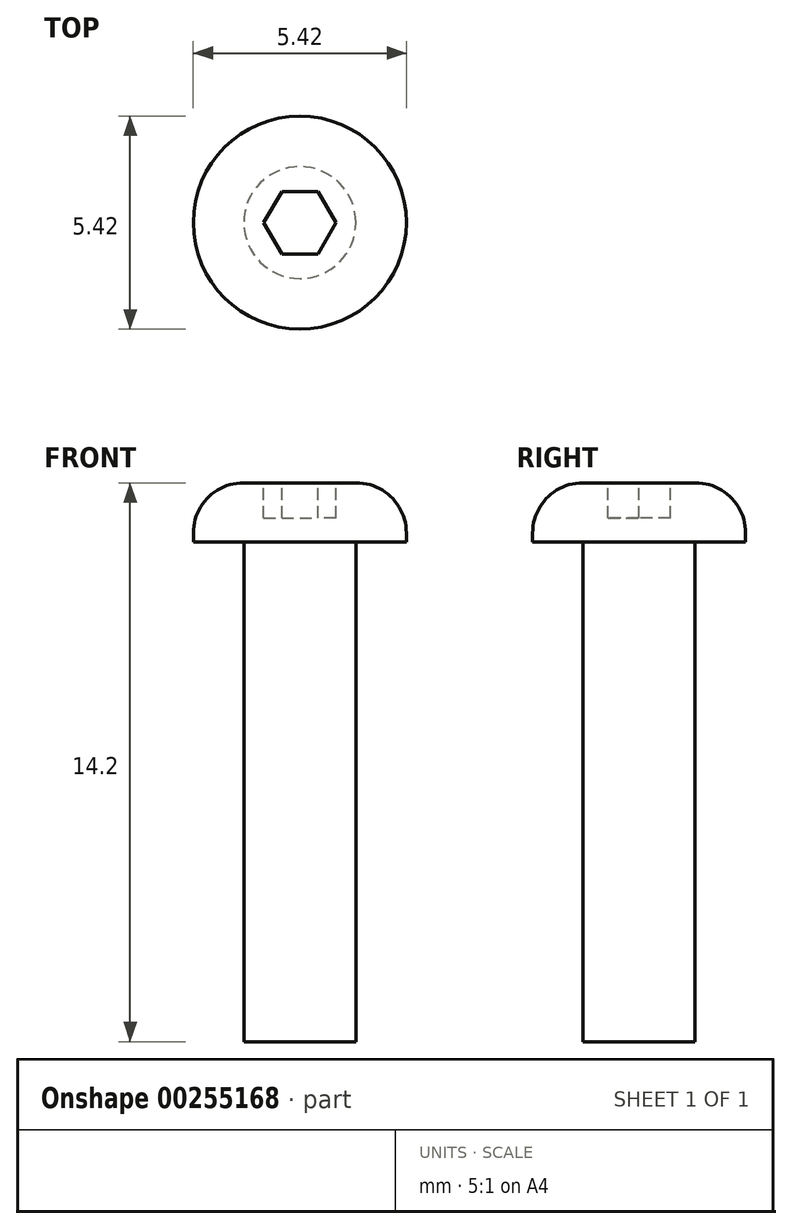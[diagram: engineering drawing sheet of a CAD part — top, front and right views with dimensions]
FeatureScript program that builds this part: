
annotation { "Feature Type Name" : "Feature", "Feature Type Description" : "" }
export const myFeature = defineFeature(function(context is Context, id is Id, definition is map)
    precondition{}
    {
        {
            var Q0;
            Q0=qCreatedBy(makeId("Top.planeOp"),FACE);
            var sketch = newSketch(context, id + "F0", { "sketchPlane" : qUnion([Q0])});
            skCircle(sketch, "E0", {"center": v(0, 0) * mm, "radius": 1.42 * mm});
            skSolve(sketch);
        }
        {
            var Q0;
            Q0 = qSketchRegion(id + "F0", true);
            extrude(context, id + "F1", {"entities" : qUnion([Q0]), "depth" : 12.7 * mm});
        }
        {
            var Q0;
            Q0=makeQuery(id+"F1.opExtrude","CAP_FACE",FACE,{"disambiguationData":[OSD([sQuery(id+"F0.wireOp",EDGE,"E0")])],"isStart":false});
            var sketch = newSketch(context, id + "F2", { "sketchPlane" : qUnion([Q0])});
            skCircle(sketch, "E1", {"center": v(0, 0) * mm, "radius": 2.7 * mm});
            skSolve(sketch);
        }
        {
            var Q0;
            Q0 = qSketchRegion(id + "F2", true);
            extrude(context, id + "F3", {"entities" : qUnion([Q0]), "operationType" : NewBodyOperationType.ADD, "depth" : 1.5 * mm});
        }
        {
            var Q0;
            Q0=makeQuery(id+"F3.opExtrude","CAP_EDGE",EDGE,{"disambiguationData":[OSD([sQuery(id+"F2.wireOp",EDGE,"E1")])],"isStart":false});
            fillet(context, id + "F4", {"entities" : qUnion([Q0]), "radius" : 1.27 * mm, "tangentPropagation" : true, "allowEdgeOverflow" : false});
        }
        {
            var Q0;
            Q0=makeQuery(id+"F3.opExtrude","CAP_FACE",FACE,{"disambiguationData":[OSD([sQuery(id+"F2.wireOp",EDGE,"E1")])],"isStart":false});
            var sketch = newSketch(context, id + "F5", { "sketchPlane" : qUnion([Q0])});
            skCircle(sketch, "E2.cCircle", {"center": v(0, 0) * mm, "radius": 0.8 * mm, "construction": true});
            skLineSegment(sketch, "E2.0", {"start": v(0.92, 0) * mm, "end": v(0.46, -0.8) * mm});
            skLineSegment(sketch, "E2.1", {"start": v(0.46, -0.8) * mm, "end": v(-0.46, -0.8) * mm});
            skLineSegment(sketch, "E2.2", {"start": v(-0.46, -0.8) * mm, "end": v(-0.92, 0) * mm});
            skLineSegment(sketch, "E2.3", {"start": v(-0.92, 0) * mm, "end": v(-0.46, 0.8) * mm});
            skLineSegment(sketch, "E2.4", {"start": v(-0.46, 0.8) * mm, "end": v(0.46, 0.8) * mm});
            skLineSegment(sketch, "E2.5", {"start": v(0.46, 0.8) * mm, "end": v(0.92, 0) * mm});
            skPoint(sketch, "E2.0.midPoint", {"position": v(0.69, -0.4) * mm});
            skSolve(sketch);
        }
        {
            var Q0;
            Q0 = qSketchRegion(id + "F5", true);
            extrude(context, id + "F6", {"entities" : qUnion([Q0]), "operationType" : NewBodyOperationType.REMOVE, "oppositeDirection" : true, "depth" : 0.9 * mm});
        }
    });
